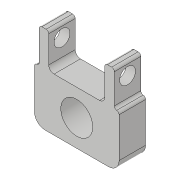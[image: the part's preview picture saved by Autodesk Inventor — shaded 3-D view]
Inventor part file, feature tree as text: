
AUTODESK INVENTOR PART (.ipt)
format: ipt  version: 2018.3 (Build 223284000, 284)  size: 152,064 bytes
history: native  units: in
note: dims shown in document units (in); Inventor stores cm internally (conversion verified against a paired STEP export)
features: extrude x4, fillet x3, sketch x3
ambient origin geometry x8: Origin, YZ Plane, XZ Plane, XY Plane, X Axis, Y Axis, Z Axis, Center Point
bodies: Solid1 (feature_tree)
feature tree (10):
  extrude  "Extrusion1"  Depth=0.225in
  extrude  "Extrusion2"  Depth=0.625in TaperAngle=0.0deg
  extrude  "Extrusion3"  Depth=1.325in TaperAngle=0.0deg
  fillet  "Fillet2"  Radius=0.375in
  fillet  "Fillet4"  Radius=0.3in
  fillet  "Fillet5"  Radius=0.5in
  extrude  "Extrusion4"  Depth=0.25in
  sketch  "Sketch1"  dims[d1=1.25in d4=0.225in]
  sketch  "Sketch2"  dims[d5=0.225in d7=0.625in d8=0.0in]
  sketch  "Sketch4"  dims[d10=0.755in d11=0.5in d12=0.0in d13=0.375in d15=0.3in d16=0.5in d17=0.0in d19=0.25in d21=0.825in d22=0.0625in d23=0.125in d24=0.625in d26=0.375in d27=1.0in d28=0.0in d31=1.0in d32=2.0in d35=0.1125in d37=0.1125in d38=1.325in]
